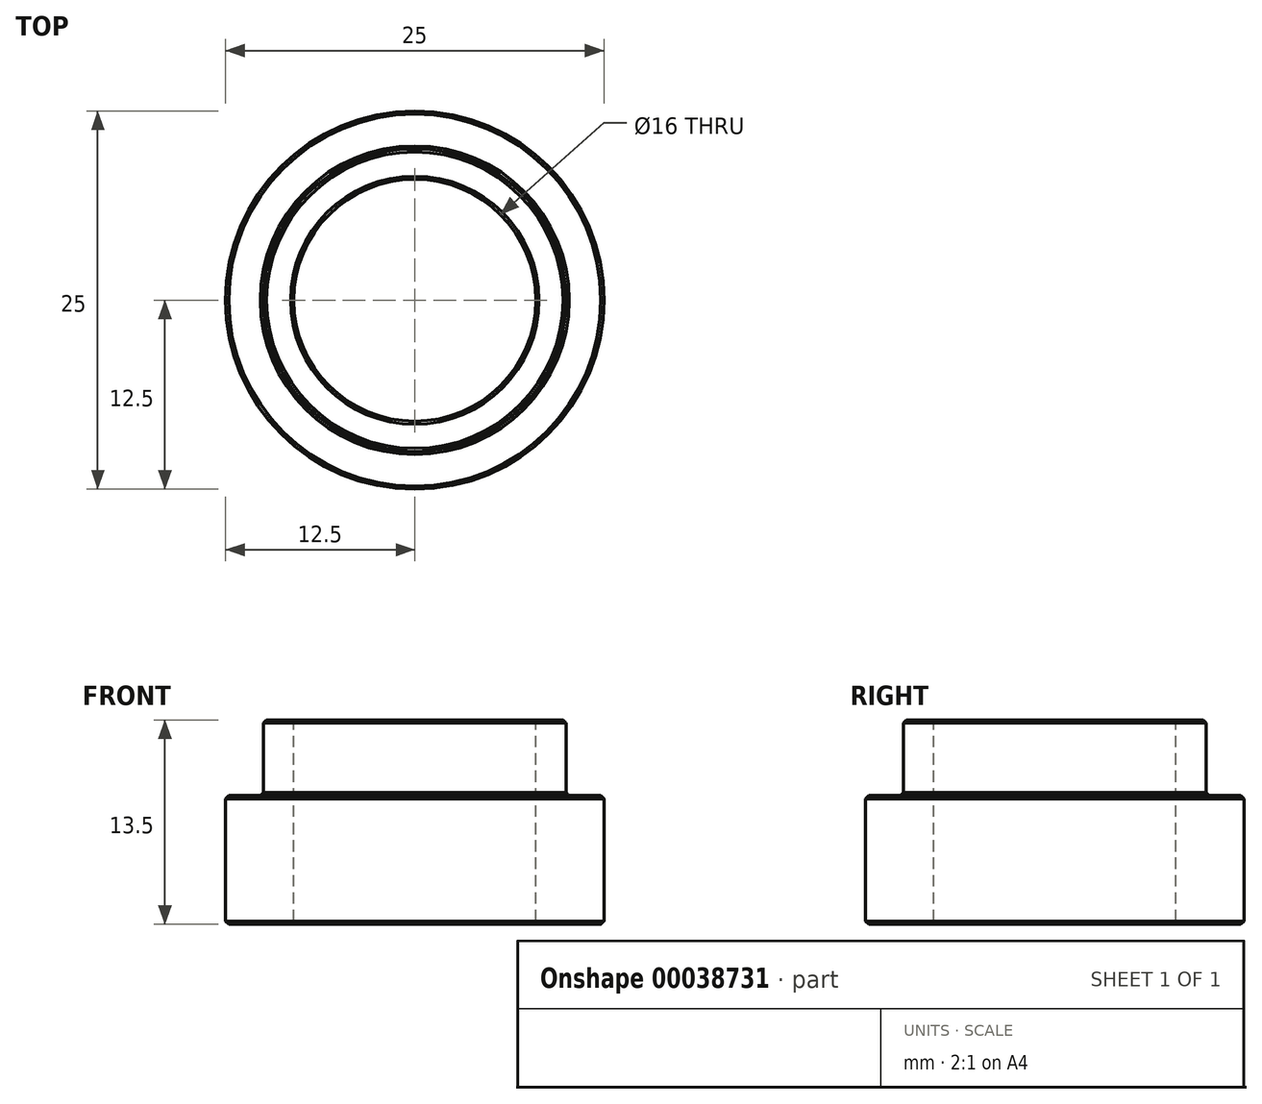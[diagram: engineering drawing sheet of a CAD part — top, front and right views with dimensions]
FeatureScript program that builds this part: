
annotation { "Feature Type Name" : "Feature", "Feature Type Description" : "" }
export const myFeature = defineFeature(function(context is Context, id is Id, definition is map)
    precondition{}
    {
        {
            var Q0;
            Q0=qCreatedBy(makeId("Top.planeOp"),FACE);
            var sketch = newSketch(context, id + "F0", { "sketchPlane" : qUnion([Q0])});
            skCircle(sketch, "E0", {"center": v(0, 0) * mm, "radius": 12.5 * mm});
            skSolve(sketch);
        }
        {
            var Q0;
            Q0=makeQuery(id+"F0.imprint","IMPRINT",FACE,{"disambiguationData":[TD([[makeQuery(id+"F0.imprint","IMPRINT",EDGE,{"derivedFrom":sQuery(id+"F0.wireOp",EDGE,"E0")}),1.0]])]});
            extrude(context, id + "F1", {"entities" : qUnion([Q0]), "depth" : 8.5 * mm});
        }
        {
            var Q0;
            Q0=makeQuery(id+"F1.opExtrude","CAP_FACE",FACE,{"disambiguationData":[OSD([sQuery(id+"F0.wireOp",EDGE,"E0")])],"isStart":false});
            var sketch = newSketch(context, id + "F2", { "sketchPlane" : qUnion([Q0])});
            skCircle(sketch, "E1", {"center": v(0, 0) * mm, "radius": 10 * mm});
            skSolve(sketch);
        }
        {
            var Q0;
            Q0=makeQuery(id+"F2.imprint","IMPRINT",FACE,{"disambiguationData":[TD([[makeQuery(id+"F2.imprint","IMPRINT",EDGE,{"derivedFrom":sQuery(id+"F2.wireOp",EDGE,"E1")}),1.0]])]});
            extrude(context, id + "F3", {"entities" : qUnion([Q0]), "operationType" : NewBodyOperationType.ADD, "depth" : 5 * mm});
        }
        {
            var Q0;
            Q0=makeQuery(id+"F3.opExtrude","CAP_FACE",FACE,{"disambiguationData":[OSD([sQuery(id+"F2.wireOp",EDGE,"E1")])],"isStart":false});
            var sketch = newSketch(context, id + "F4", { "sketchPlane" : qUnion([Q0])});
            skCircle(sketch, "E2", {"center": v(0, 0) * mm, "radius": 8 * mm});
            skSolve(sketch);
        }
        {
            var Q0;
            Q0=makeQuery(id+"F4.imprint","IMPRINT",FACE,{"disambiguationData":[TD([[makeQuery(id+"F4.imprint","IMPRINT",EDGE,{"derivedFrom":sQuery(id+"F4.wireOp",EDGE,"E2")}),1.0]])]});
            extrude(context, id + "F5", {"entities" : qUnion([Q0]), "operationType" : NewBodyOperationType.REMOVE, "endBound" : BoundingType.THROUGH_ALL, "oppositeDirection" : true, "depth" : 25 * mm});
        }
        {
            var Q0;
            Q0=makeQuery(id+"F3.opExtrude","CAP_FACE",FACE,{"disambiguationData":[OSD([sQuery(id+"F2.wireOp",EDGE,"E1")])],"isStart":false});
            var Q1;
            Q1=makeQuery(id+"F1.opExtrude","CAP_FACE",FACE,{"disambiguationData":[OSD([sQuery(id+"F0.wireOp",EDGE,"E0")])],"isStart":false});
            var Q2;
            Q2=makeQuery(id+"F1.opExtrude","CAP_FACE",FACE,{"disambiguationData":[OSD([sQuery(id+"F0.wireOp",EDGE,"E0")])],"isStart":true});
            chamfer(context, id + "F6", {"entities" : qUnion([Q0, Q1, Q2]), "width" : 0.2 * mm, "tangentPropagation" : true});
        }
    });
